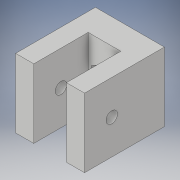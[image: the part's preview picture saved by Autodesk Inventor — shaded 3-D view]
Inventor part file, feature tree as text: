
AUTODESK INVENTOR PART (.ipt)
format: ipt  version: 2019 (Build 230136000, 136)  size: 281,088 bytes
history: native  units: in
note: dims shown in document units (in); Inventor stores cm internally (conversion verified against a paired STEP export)
features: extrude x5, sketch x5, projected_geometry x1
ambient origin geometry x8: Origin, YZ Plane, XZ Plane, XY Plane, X Axis, Y Axis, Z Axis, Center Point
bodies: Solid1 (feature_tree)
feature tree (11):
  extrude  "Extrusion1"  Depth=0.748in
  extrude  "Extrusion2"  Depth=0.3543in
  extrude  "Extrusion3"  Depth=0.5906in
  extrude  "Extrusion4"  Depth=0.5906in
  extrude  "Extrusion5"  Depth=0.126in
  sketch  "Sketch1"  dims[d0=0.748in d1=0.748in]
  sketch  "Sketch2"  dims[d2=0.2756in d3=0.0in d4=0.3543in]
  projected_geometry  "Projected Loop1"
  sketch  "Sketch3"  dims[d5=0.5906in d6=0.0in d7=0.1673in]
  sketch  "Sketch4"  dims[d8=0.5906in d9=0.0in d10=0.124in]
  sketch  "Sketch5"  dims[d11=0.5906in d12=0.0in d13=0.3248in d14=0.126in d15=0.0in]
